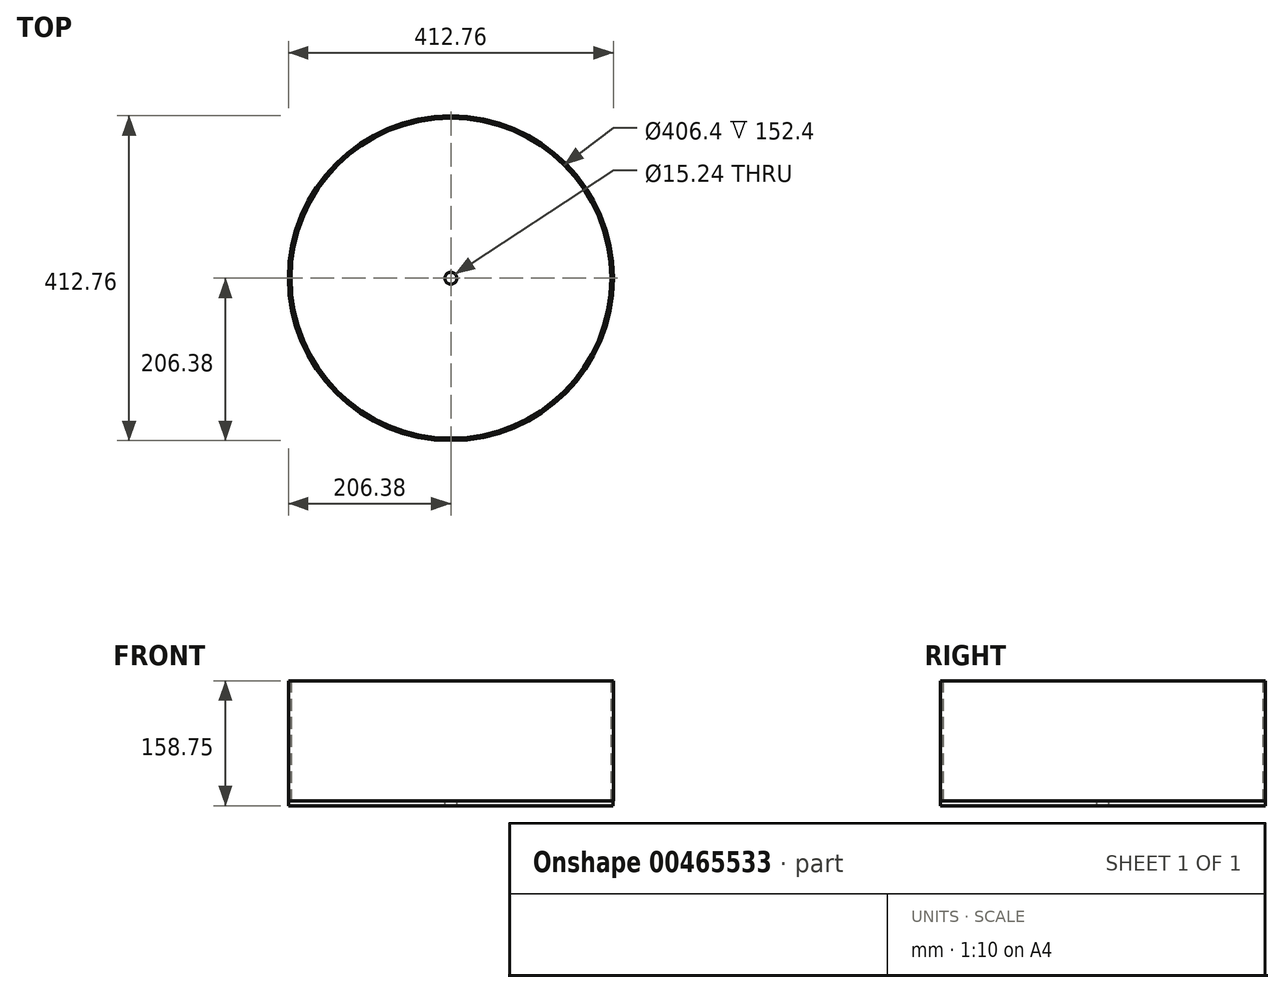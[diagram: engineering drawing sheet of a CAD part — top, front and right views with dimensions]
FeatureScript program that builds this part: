
annotation { "Feature Type Name" : "Feature", "Feature Type Description" : "" }
export const myFeature = defineFeature(function(context is Context, id is Id, definition is map)
    precondition{}
    {
        {
            var Q0;
            Q0=qCreatedBy(makeId("Top.planeOp"),FACE);
            var sketch = newSketch(context, id + "F0", { "sketchPlane" : qUnion([Q0])});
            skCircle(sketch, "E0", {"center": v(0, 0) * mm, "radius": 203.2 * mm});
            skCircle(sketch, "E1", {"center": v(0, 0) * mm, "radius": 206.38 * mm});
            skSolve(sketch);
        }
        {
            var Q0;
            Q0 = qSketchRegion(id + "F0", true);
            extrude(context, id + "F1", {"entities" : qUnion([Q0]), "depth" : 152.4 * mm});
        }
        {
            var Q0;
            Q0=qCreatedBy(makeId("Top.planeOp"),FACE);
            var sketch = newSketch(context, id + "F2", { "sketchPlane" : qUnion([Q0])});
            skCircle(sketch, "E2", {"center": v(0, 0) * mm, "radius": 206.17 * mm});
            skSolve(sketch);
        }
        {
            var Q0;
            Q0 = qSketchRegion(id + "F2", true);
            extrude(context, id + "F3", {"entities" : qUnion([Q0]), "operationType" : NewBodyOperationType.ADD, "oppositeDirection" : true, "depth" : 6.35 * mm});
        }
        {
            var Q0;
            Q0=makeQuery(id+"F3.opExtrude","CAP_FACE",FACE,{"disambiguationData":[OSD([sQuery(id+"F2.wireOp",EDGE,"E2")])],"isStart":true});
            var sketch = newSketch(context, id + "F4", { "sketchPlane" : qUnion([Q0])});
            skCircle(sketch, "E3", {"center": v(0, 0) * mm, "radius": 7.62 * mm});
            skSolve(sketch);
        }
        {
            var Q0;
            Q0 = qSketchRegion(id + "F4", true);
            extrude(context, id + "F5", {"entities" : qUnion([Q0]), "operationType" : NewBodyOperationType.REMOVE, "oppositeDirection" : true, "depth" : 25.4 * mm});
        }
    });
